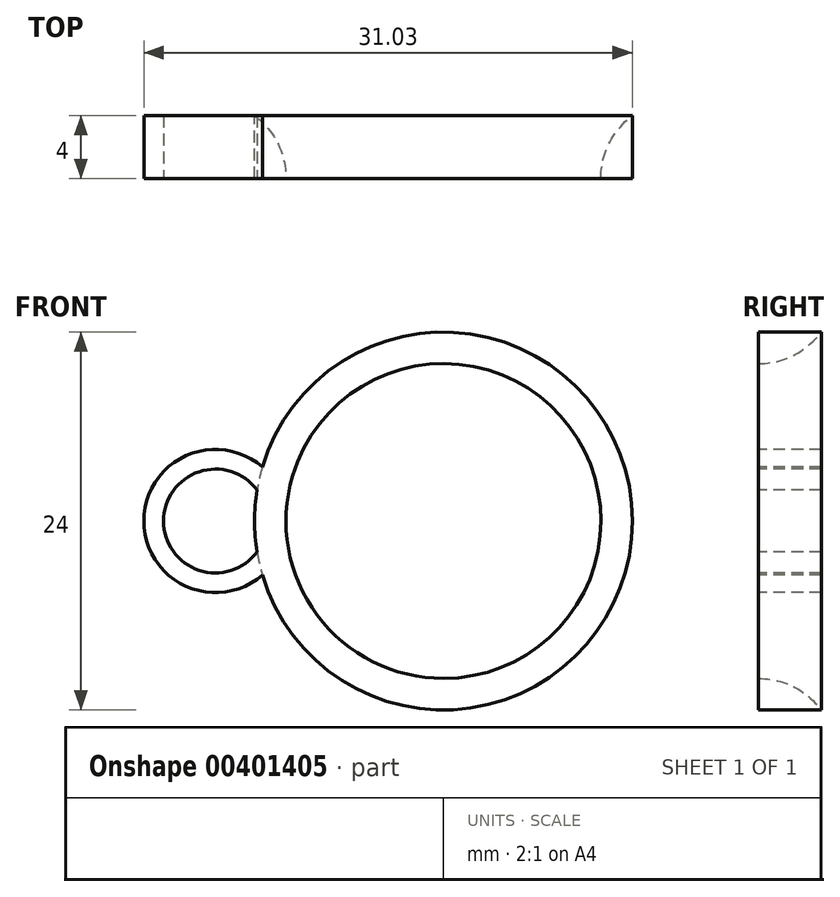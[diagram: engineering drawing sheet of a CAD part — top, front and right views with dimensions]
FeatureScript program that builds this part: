
annotation { "Feature Type Name" : "Feature", "Feature Type Description" : "" }
export const myFeature = defineFeature(function(context is Context, id is Id, definition is map)
    precondition{}
    {
        {
            assignVariable(context, id + "F0", {"name" : "RingThickness", "anyValue" : 4 * mm});
        }
        {
            var Q0;
            Q0=qCreatedBy(makeId("Front.planeOp"),FACE);
            var sketch = newSketch(context, id + "F1", { "sketchPlane" : qUnion([Q0])});
            skCircle(sketch, "E0", {"center": v(0, 0) * mm, "radius": 12 * mm});
            skCircle(sketch, "E1", {"center": v(0, 0) * mm, "radius": 10 * mm});
            skLineSegment(sketch, "E2", {"start": v(-10, 0) * mm, "end": v(-10, -25.72) * mm, "construction": true});
            skSolve(sketch);
        }
        {
            var Q0;
            Q0=makeQuery(id+"F1.imprint","IMPRINT",FACE,{"disambiguationData":[TD([[makeQuery(id+"F1.imprint","IMPRINT",EDGE,{"derivedFrom":sQuery(id+"F1.wireOp",EDGE,"E0")}),1.0]])]});
            extrude(context, id + "F2", {"entities" : qUnion([Q0]), "depth" : getVariable(context, 'RingThickness')});
        }
        {
            var Q0;
            Q0=makeQuery(id+"F2.opExtrude","CAP_EDGE",EDGE,{"disambiguationData":[OSD([sQuery(id+"F1.wireOp",EDGE,"E1")])],"isStart":true});
            fillet(context, id + "F3", {"entities" : qUnion([Q0]), "radius" : 5 * mm, "tangentPropagation" : true, "allowEdgeOverflow" : false});
        }
        {
            var Q0;
            Q0=makeQuery(id+"F2.opExtrude","CAP_FACE",FACE,{"disambiguationData":[OSD([sQuery(id+"F1.wireOp",EDGE,"E0"),sQuery(id+"F1.wireOp",EDGE,"E1")])],"isStart":false});
            var sketch = newSketch(context, id + "F4", { "sketchPlane" : qUnion([Q0])});
            skArc(sketch, "E3", {"start": v(-11.5, 3.43) * mm, "mid": v(-19.03, 0) * mm, "end": v(-11.5, -3.43) * mm});
            skArc(sketch, "E4", {"start": v(-11.84, 1.97) * mm, "mid": v(-17.78, 0) * mm, "end": v(-11.84, -1.97) * mm});
            skLineSegment(sketch, "E5", {"start": v(-17.78, 9.85) * mm, "end": v(-17.78, -10.33) * mm, "construction": true});
            skPoint(sketch, "E5.startSnap0", {"position": v(-17.78, 0) * mm});
            skLineSegment(sketch, "E6", {"start": v(0, -4.99) * mm, "end": v(0, 6.57) * mm, "construction": true});
            skSolve(sketch);
        }
        {
            var Q0;
            {var subQ0=sQuery(id+"F4.wireOp",EDGE,"E3");Q0=makeQuery(id+"F4.imprint","IMPRINT",FACE,{"disambiguationData":[TD([[makeQuery(id+"F4.imprint","IMPRINT",EDGE,{"derivedFrom":subQ0}),1.0]])]});}
            var Q1;
            Q1=makeQuery(id+"F3.opFillet","BLEND_FACE",FACE,{"disambiguationData":[OSD([sQuery(id+"F1.wireOp",EDGE,"E1")])]});
            extrude(context, id + "F5", {"entities" : qUnion([Q0]), "operationType" : NewBodyOperationType.ADD, "oppositeDirection" : true, "endBoundEntityFace" : qUnion([Q1]), "depth" : getVariable(context, 'RingThickness')});
        }
    });
